# Revit family: wagenfeldlampe
name_source: partatom
category: Leuchten
units: mm (PartAtom-declared; Revit-internal decimal feet)

## family parameters
Arbeitsebenenbasiert = Nein
Beim Laden mit Abzugskörper schneiden = Nein
Bemaßung runder Anschluss = Durchmesser verwenden
Beschriftungsausrichtung beibehalten = Nein
Gemeinsam genutzt = Nein
Immer vertikal = Ja
Lichtquelle = Ja
Raumberechnungspunkt = Nein
Teiletyp = Normal

## types (1)
- Wagenfeld
    Dicke Sockel = 20 mm  [stored 0.0656168 ft]
    Farbfilter = 16777215
    Farbtemperaturverschiebung bei Dämpfen der Lampe = <Keine Auswahl>
    Glocke = Glas, weiß, hohe Luminanz
    Größe des Lichtquellensymbols = 300 mm
    H = 360 mm  [stored 1.1811 ft]
    Kommentare zu Wattzahl = 250
    Lampe = Halogen
    R aussen = 80 mm  [stored 0.262467 ft]
    R innen = 75 mm
    Radius Fuß = 12 mm  [stored 0.0393701 ft]
    Radius Schirm unten = 60 mm  [stored 0.19685 ft]
    Radius Sockel = 80 mm  [stored 0.262467 ft]
    Standfuß = <Nach Kategorie>
    Vorgabe-Ansicht = 0 mm  [stored 0 ft]

note: [stored X ft] marks values corroborated as IEEE doubles in the binary element streams (Revit-internal decimal feet)
